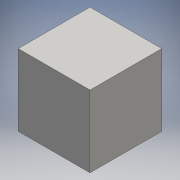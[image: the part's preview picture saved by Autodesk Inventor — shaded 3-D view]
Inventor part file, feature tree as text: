
AUTODESK INVENTOR PART (.ipt)
format: ipt  version: 2016 (Build 200138000, 138)  size: 79,872 bytes
history: native  units: mm
features: extrude x1, sketch x1
ambient origin geometry x8: Origin, YZ Plane, XZ Plane, XY Plane, X Axis, Y Axis, Z Axis, Center Point
bodies: Solid1 (feature_tree)
feature tree (2):
  extrude  "Extrusion1"  Depth=15.0mm
  sketch  "Sketch1"  dims[d0=15.0mm d1=15.0mm d2=15.0mm d3=0.0mm]
